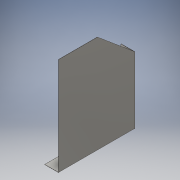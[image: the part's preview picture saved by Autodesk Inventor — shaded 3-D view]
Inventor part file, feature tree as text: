
AUTODESK INVENTOR PART (.ipt)
format: ipt  version: 2016 (Build 200138000, 138)  size: 177,664 bytes
history: native  units: mm
features: sheet_metal_op x7, sketch x4, other x4, extrude x1
ambient origin geometry x8: Origin, YZ Plane, XZ Plane, XY Plane, X Axis, Y Axis, Z Axis, Center Point
bodies: Solid1 (feature_tree)
feature tree (16):
  sheet_metal_op  "Face1"
  sheet_metal_op  "Flange2"
  extrude  "Extrusion1"  Depth=350.0mm
  sheet_metal_op  "Flange3"
  sketch  "Sketch1"  dims[d0=472.0mm d1=350.0mm]
  other  "Plate1"
  sketch  "Sketch3"  dims[d2=22.68928mm]
  other  "Plate3"
  sheet_metal_op  "Bend2"
  sheet_metal_op  "Corner2"
  sketch  "Sketch4"  dims[d3=550.0mm]
  sketch  "Sketch5"  dims[d4=350.0mm d5=24.43461mm d6=252.0mm d8=22.340214mm d9=1.6mm d20=1.6mm d21=0.8mm d22=3.2mm d23=1.6mm d24=100.0mm d25=90.0deg d26=1.6mm d27=6.4mm d28=1.6mm d29=1.6mm d30=170.5mm d31=0.0mm d32=1.6mm d33=0.8mm d34=3.2mm d35=1.6mm d36=100.0mm d37=90.0deg d38=1.6mm d39=6.4mm d40=1.6mm d41=1.6mm]
  other  "Plate4"
  sheet_metal_op  "Bend3"
  sheet_metal_op  "Corner3"
  other  "Definition1"
